# Revit family: IS_Tesi_T5522_BIM_NL
name_source: partatom
category: Plumbing Fixtures
units: mm (PartAtom-declared; Revit-internal decimal feet)

## family parameters
Always vertical = No
Cut with Voids When Loaded = No
OmniClass Number = 23.45.05.21.11.11
OmniClass Title = Water Operated Water Closets
Part Type = Normal
Room Calculation Point = No
Round Connector Dimension = Use Diameter
Shared = No
Work Plane-Based = No

## types (3) — shared parameters
Afmetingen = 50 x 450 x 368 mm
AfstandsEenheid = Millimeter
Auteur = Ideal Standard
BIMobject category = Toilet Seats
BIMobject category code = toilet-seats
BIMobject main category = Sanitary
BIMobject main category code = sanitary
Beschrijvinggarantie = Herstellergarantie
BimObjectNaam = IS_IdealStandard_WCseatsandcovers_Tesi_T5522_IdealStandard
Brand url = https://www.idealstandard.nl
Breedte = 367.914566
Date of publishing = 15/03/2023
Diepte = 448 mm
DuurEenheid = Jahre
Edition number = 1
Garantieonderdelen = https://www.idealstandard.nl
Garantieunits = Jahre
GemaaktOp = 15/03/2023
Hoogte = 48,6017451286316
Hulp = https://www.idealstandard.nl
IFC Classification = Sanitary Terminal
IfcExportAs = IfcSanitaryTerminalType
IfcExportType = WCSEAT
Installatieinstructies = https://www.idealstandard.nl
Installation instructions = https://www.idealstandard.nl
Lengte = 448 mm
Manufacturer = Ideal Standard
Manufacturer name = Ideal Standard
Masterformat 2014 Code = 10 28 13
Masterformat 2014 Description = Toilet Accessories
Materiaal = Duroplast
MateriaalWC = Duroplast
Material main = Duroplast
Merk = Ideal Standard
Montageinstuctie = https://www.idealstandard.nl
NBS Reference Code = 45-35-70/391
NBS Reference Description = WC seats and covers
Nettogewicht = 2.4
NominalHeight = 49 mm
NominalLength = 448 mm
NominalWidth = 368 mm
OmniClass Code = 23-31 19 19 17
OmniClass Description = Water Closet Seats
OppervlakteEenheid = Millimeter
Product Guid = 10100610-76e5-4473-9699-47c79dacce56
Product SKU = T5522
Product certification = https://www.idealstandard.nl
Product data url = https://bimobject.com
Product family = TESI
Product group = Tesi
Product name = TESI S&C SW SC TO FOR EASYFIX
Product url = https://www.idealstandard.nl
Productinformatie = https://www.idealstandard.nl
QR code = http://bimobject.com
Revisie = 1
Size = 50 x 450 x 368mm
Technical description = https://www.idealstandard.nl
Telefoonnummer = 077 355 08 08
Toepassing = WC Seat & Cover
Typeconnectie = Installation
UNSPSC Code = 301815
URL = https://www.idealstandard.nl
Uniclass 2015 Code = Pr_40_20_93_95
Uniclass 2015 Name = WC seats and covers
Uniclass2015Beschrijving = WC seats and covers
Uniclass2015Referentie = Pr_40_20_93_95
Uniclass2015Version = v1.26
Uniformat II Code = D2010
Uniformat II Description = Plumbing Fixtures
Urlproducent = https://www.idealstandard.nl
ValutaEenheid = Euro
Versie = 1
Verwachtelevensduur = 5
Volumeunits = Liter
Vorm = geformt
Wisselstukken = https://www.idealstandard.nl
Youtube clip = https://www.youtube.com
zero-valued in all types: BrutoGewicht, Cost, Default Elevation, Vervangingskosten

## per-type parameters (varying)
| type | Afwerking | Artikelnummer | Artikelomschrijving | Artikelreferentie | Barcode | Description | Eigenschappen | GTIN code | Kleur | Model | Referentie |
| T552201 - Tesi seat & cover soft close, sandwich, Quick release for EASY FIX+ bowl, in white | Weiß | T552201 | Ideal Standard Tesi Sitz & Deckel mit Soft-Close, Sandwich, Schnellverschluss für EASY FIX+ Schüssel, in Weiß | T552201 | 8014140515098 | Tesi Sitz & Deckel mit Soft-Close, Sandwich, Schnellverschluss für EASY FIX+ Schüssel, in Weiß | Sitz & Deckel mit Soft-Close, Sandwich, Schnellverschluss für EASY FIX+ Schüssel, in Weiß | 8014140515098 | Weiß | T552201 | Ideal Standard Tesi Sitz & Deckel mit Soft-Close, Sandwich, Schnellverschluss für EASY FIX+ Schüssel, in Weiß |
| T5522V1 - Tesi seat & cover soft close, sandwich, Quick release for EASY FIX+ bowl, in SILK WHITE | Seidenweiß | T5522V1 | Ideal Standard Tesi Sitz & Deckel mit Soft-Close, Sandwich, Schnellverschluss für EASY FIX+ Schüssel, in Seidenweiß | T5522V1 | 8014140515104 | Tesi Sitz & Deckel mit Soft-Close, Sandwich, Schnellverschluss für EASY FIX+ Schüssel, in Seidenweiß | Sitz & Deckel mit Soft-Close, Sandwich, Schnellverschluss für EASY FIX+ Schüssel, in Seidenweiß | 8014140515104 | Seidenweiß | T5522V1 | Ideal Standard Tesi Sitz & Deckel mit Soft-Close, Sandwich, Schnellverschluss für EASY FIX+ Schüssel, in Seidenweiß |
| T5522V3 - Tesi seat & cover soft close, sandwich, Quick release for EASY FIX+ bowl, in SILK BLACK | Seidenschwarz | T5522V3 | Ideal Standard Tesi Sitz & Deckel mit Soft-Close, Sandwich, Schnellverschluss für EASY FIX+ Schüssel, in Seidenschwarz | T5522V3 | 8014140515111 | Tesi Sitz & Deckel mit Soft-Close, Sandwich, Schnellverschluss für EASY FIX+ Schüssel, in Seidenschwarz | Sitz & Deckel mit Soft-Close, Sandwich, Schnellverschluss für EASY FIX+ Schüssel, in Seidenschwarz | 8014140515111 | Seidenschwarz | T5522V3 | Ideal Standard Tesi Sitz & Deckel mit Soft-Close, Sandwich, Schnellverschluss für EASY FIX+ Schüssel, in Seidenschwarz |

## geometry (parser evidence)
native form markers: Blend x4, Sweep x2
no freeform markers — native parametric forms only
